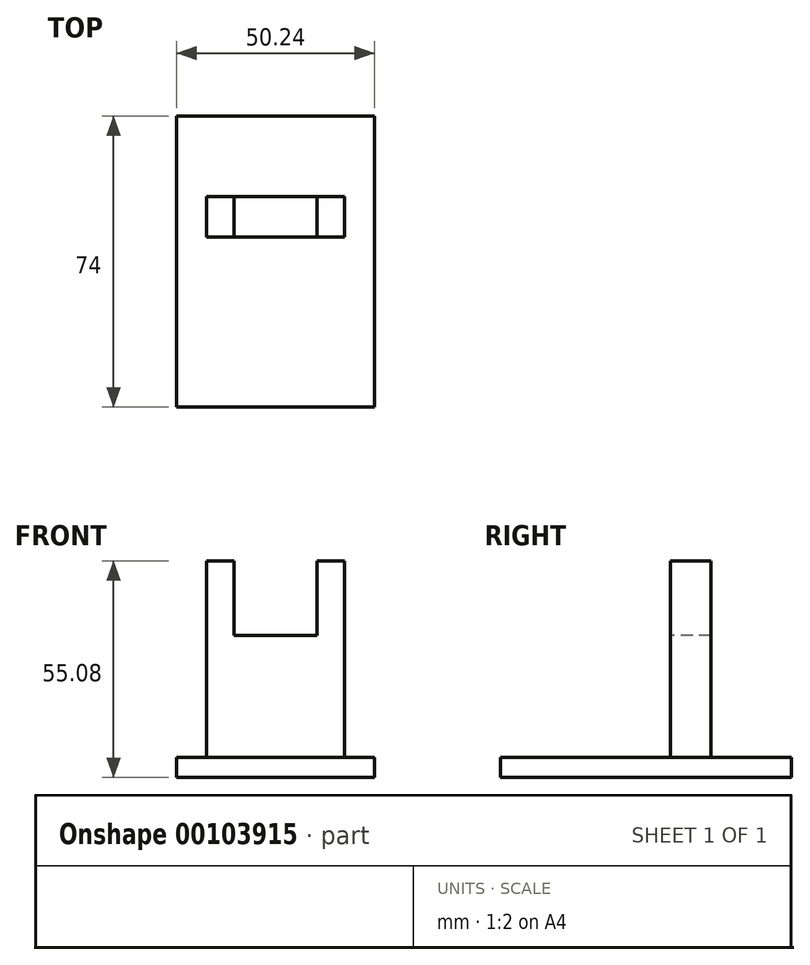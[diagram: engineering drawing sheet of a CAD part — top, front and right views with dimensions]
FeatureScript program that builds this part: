
annotation { "Feature Type Name" : "Feature", "Feature Type Description" : "" }
export const myFeature = defineFeature(function(context is Context, id is Id, definition is map)
    precondition{}
    {
        {
            var Q0;
            Q0=qCreatedBy(makeId("Front.planeOp"),FACE);
            var sketch = newSketch(context, id + "F0", { "sketchPlane" : qUnion([Q0])});
            skLineSegment(sketch, "E0.bottom", {"start": v(17.5, 25) * mm, "end": v(-17.5, 25) * mm});
            skLineSegment(sketch, "E0.top", {"start": v(17.5, -25) * mm, "end": v(-17.5, -25) * mm});
            skLineSegment(sketch, "E0.left", {"start": v(17.5, 25) * mm, "end": v(17.5, -25) * mm});
            skLineSegment(sketch, "E0.right", {"start": v(-17.5, 25) * mm, "end": v(-17.5, -25) * mm});
            skPoint(sketch, "E0.middle", {"position": v(0, 0) * mm});
            skSolve(sketch);
        }
        {
            var Q0;
            Q0 = qSketchRegion(id + "F0", true);
            extrude(context, id + "F1", {"entities" : qUnion([Q0]), "depth" : 10.25 * mm});
        }
        {
            var Q0;
            Q0=makeQuery(id+"F1.opExtrude","CAP_FACE",FACE,{"disambiguationData":[OSD([sQuery(id+"F0.wireOp",EDGE,"E0.bottom"),sQuery(id+"F0.wireOp",EDGE,"E0.top"),sQuery(id+"F0.wireOp",EDGE,"E0.left"),sQuery(id+"F0.wireOp",EDGE,"E0.right")])],"isStart":false});
            var sketch = newSketch(context, id + "F2", { "sketchPlane" : qUnion([Q0])});
            skLineSegment(sketch, "E1.bottom", {"start": v(-10.5, 25) * mm, "end": v(10.5, 25) * mm});
            skLineSegment(sketch, "E1.top", {"start": v(-10.5, 6) * mm, "end": v(10.5, 6) * mm});
            skLineSegment(sketch, "E1.left", {"start": v(-10.5, 25) * mm, "end": v(-10.5, 6) * mm});
            skLineSegment(sketch, "E1.right", {"start": v(10.5, 25) * mm, "end": v(10.5, 6) * mm});
            skSolve(sketch);
        }
        {
            var Q0;
            Q0 = qSketchRegion(id + "F2", true);
            extrude(context, id + "F3", {"entities" : qUnion([Q0]), "operationType" : NewBodyOperationType.REMOVE, "oppositeDirection" : true, "depth" : 25 * mm});
        }
        {
            var Q0;
            Q0=makeQuery(id+"F1.opExtrude","SWEPT_FACE",FACE,{"disambiguationData":[OSD([sQuery(id+"F0.wireOp",EDGE,"E0.top")])]});
            cPlane(context, id + "F4", {"entities" : qUnion([Q0]), "cplaneType" : CPlaneType.OFFSET, "offset" : 0 * mm, "width" : 150 * mm, "height" : 150 * mm});
        }
        {
            var Q0;
            Q0=qCreatedBy(id+"F4.planeOp",FACE);
            var sketch = newSketch(context, id + "F5", { "sketchPlane" : qUnion([Q0])});
            skLineSegment(sketch, "E2.bottom", {"start": v(25.13, -20.5) * mm, "end": v(-25.13, -20.5) * mm});
            skLineSegment(sketch, "E2.top", {"start": v(-25.13, 53.5) * mm, "end": v(25.12, 53.5) * mm});
            skLineSegment(sketch, "E2.left", {"start": v(25.12, -20.5) * mm, "end": v(25.12, 53.5) * mm});
            skLineSegment(sketch, "E2.right", {"start": v(-25.13, -20.5) * mm, "end": v(-25.13, 53.5) * mm});
            skSolve(sketch);
        }
        {
            var Q0;
            Q0 = qSketchRegion(id + "F5", true);
            extrude(context, id + "F6", {"entities" : qUnion([Q0]), "operationType" : NewBodyOperationType.ADD, "depth" : 5.08 * mm});
        }
    });
